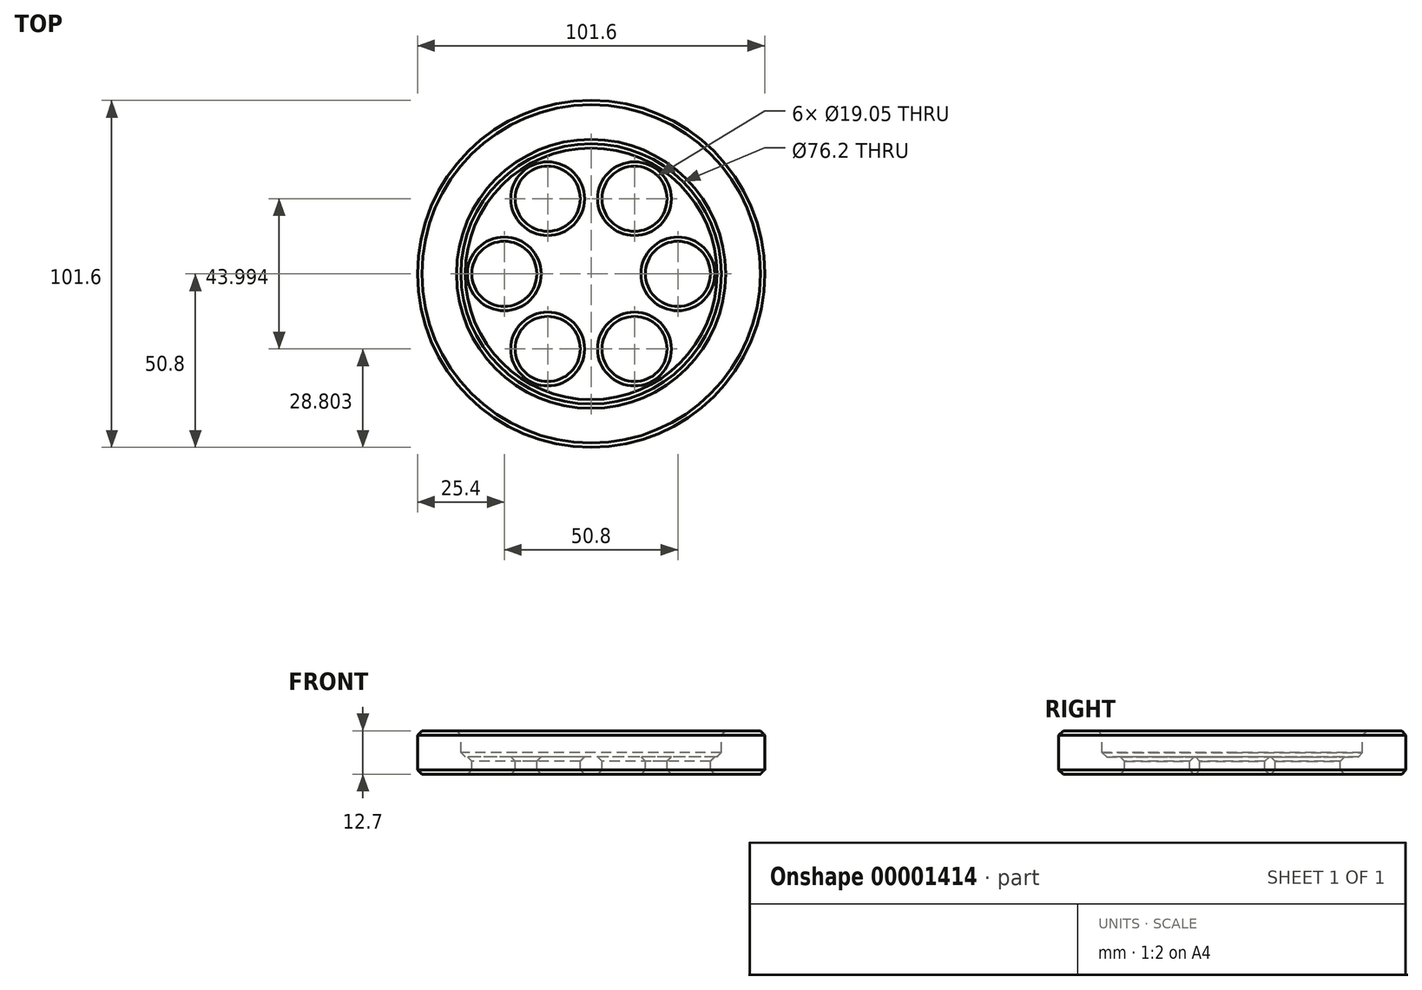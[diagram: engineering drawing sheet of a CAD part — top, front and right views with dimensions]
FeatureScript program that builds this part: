
annotation { "Feature Type Name" : "Feature", "Feature Type Description" : "" }
export const myFeature = defineFeature(function(context is Context, id is Id, definition is map)
    precondition{}
    {
        {
            var Q0;
            Q0=qCreatedBy(makeId("Top.planeOp"),FACE);
            var sketch = newSketch(context, id + "F0", { "sketchPlane" : qUnion([Q0])});
            skCircle(sketch, "E0", {"center": v(0, 0) * mm, "radius": 50.8 * mm});
            skSolve(sketch);
        }
        {
            var Q0;
            Q0 = qSketchRegion(id + "F0", true);
            extrude(context, id + "F1", {"entities" : qUnion([Q0]), "depth" : 12.7 * mm});
        }
        {
            var Q0;
            Q0=makeQuery(id+"F1.opExtrude","CAP_FACE",FACE,{"disambiguationData":[OSD([sQuery(id+"F0.wireOp",EDGE,"E0")])],"isStart":false});
            var sketch = newSketch(context, id + "F2", { "sketchPlane" : qUnion([Q0])});
            skCircle(sketch, "E1", {"center": v(0, 0) * mm, "radius": 38.1 * mm});
            skSolve(sketch);
        }
        {
            var Q0;
            Q0 = qSketchRegion(id + "F2", true);
            extrude(context, id + "F3", {"entities" : qUnion([Q0]), "operationType" : NewBodyOperationType.REMOVE, "oppositeDirection" : true, "depth" : 7.62 * mm});
        }
        {
            var Q0;
            Q0=makeQuery(id+"F3.boolean.opBoolean","COPY",FACE,{"derivedFrom":makeQuery(id+"F3.opExtrude","CAP_FACE",FACE,{"disambiguationData":[OSD([sQuery(id+"F2.wireOp",EDGE,"E1")])],"isStart":false})});
            var sketch = newSketch(context, id + "F4", { "sketchPlane" : qUnion([Q0])});
            skCircle(sketch, "E2.cCircle", {"center": v(0, 0) * mm, "radius": 22 * mm, "construction": true});
            skLineSegment(sketch, "E2.0", {"start": v(-12.7, 22) * mm, "end": v(12.7, 22) * mm, "construction": true});
            skLineSegment(sketch, "E2.1", {"start": v(12.7, 22) * mm, "end": v(25.4, 0) * mm, "construction": true});
            skLineSegment(sketch, "E2.2", {"start": v(25.4, 0) * mm, "end": v(12.7, -22) * mm, "construction": true});
            skLineSegment(sketch, "E2.3", {"start": v(12.7, -22) * mm, "end": v(-12.7, -22) * mm, "construction": true});
            skLineSegment(sketch, "E2.4", {"start": v(-12.7, -22) * mm, "end": v(-25.4, 0) * mm, "construction": true});
            skLineSegment(sketch, "E2.5", {"start": v(-25.4, 0) * mm, "end": v(-12.7, 22) * mm, "construction": true});
            skPoint(sketch, "E2.0.midPoint", {"position": v(0, 22) * mm});
            skCircle(sketch, "E3", {"center": v(-12.7, 22) * mm, "radius": 9.53 * mm});
            skCircle(sketch, "E4", {"center": v(12.7, 22) * mm, "radius": 9.53 * mm});
            skCircle(sketch, "E5", {"center": v(25.4, 0) * mm, "radius": 9.53 * mm});
            skCircle(sketch, "E6", {"center": v(12.7, -22) * mm, "radius": 9.53 * mm});
            skCircle(sketch, "E7", {"center": v(-12.7, -22) * mm, "radius": 9.53 * mm});
            skCircle(sketch, "E8", {"center": v(-25.4, 0) * mm, "radius": 9.53 * mm});
            skSolve(sketch);
        }
        {
            var Q0;
            Q0=makeQuery(id+"F4.imprint","IMPRINT",FACE,{"disambiguationData":[TD([[makeQuery(id+"F4.imprint","IMPRINT",EDGE,{"derivedFrom":sQuery(id+"F4.wireOp",EDGE,"E8")}),1.0]])]});
            var Q1;
            Q1=makeQuery(id+"F4.imprint","IMPRINT",FACE,{"disambiguationData":[TD([[makeQuery(id+"F4.imprint","IMPRINT",EDGE,{"derivedFrom":sQuery(id+"F4.wireOp",EDGE,"E3")}),1.0]])]});
            var Q2;
            Q2=makeQuery(id+"F4.imprint","IMPRINT",FACE,{"disambiguationData":[TD([[makeQuery(id+"F4.imprint","IMPRINT",EDGE,{"derivedFrom":sQuery(id+"F4.wireOp",EDGE,"E4")}),1.0]])]});
            var Q3;
            Q3=makeQuery(id+"F4.imprint","IMPRINT",FACE,{"disambiguationData":[TD([[makeQuery(id+"F4.imprint","IMPRINT",EDGE,{"derivedFrom":sQuery(id+"F4.wireOp",EDGE,"E5")}),1.0]])]});
            var Q4;
            Q4=makeQuery(id+"F4.imprint","IMPRINT",FACE,{"disambiguationData":[TD([[makeQuery(id+"F4.imprint","IMPRINT",EDGE,{"derivedFrom":sQuery(id+"F4.wireOp",EDGE,"E6")}),1.0]])]});
            var Q5;
            Q5=makeQuery(id+"F4.imprint","IMPRINT",FACE,{"disambiguationData":[TD([[makeQuery(id+"F4.imprint","IMPRINT",EDGE,{"derivedFrom":sQuery(id+"F4.wireOp",EDGE,"E7")}),1.0]])]});
            var Q6;
            Q6=sQuery(id+"F4.wireOp",EDGE,"E8");
            var Q7;
            Q7=sQuery(id+"F4.wireOp",EDGE,"E3");
            var Q8;
            Q8=sQuery(id+"F4.wireOp",EDGE,"E4");
            var Q9;
            Q9=sQuery(id+"F4.wireOp",EDGE,"E5");
            var Q10;
            Q10=sQuery(id+"F4.wireOp",EDGE,"E6");
            var Q11;
            Q11=sQuery(id+"F4.wireOp",EDGE,"E7");
            extrude(context, id + "F5", {"entities" : qUnion([Q0, Q1, Q2, Q3, Q4, Q5]), "operationType" : NewBodyOperationType.REMOVE, "surfaceEntities" : qUnion([Q6, Q7, Q8, Q9, Q10, Q11]), "oppositeDirection" : true, "depth" : 25.4 * mm});
        }
        {
            var Q0;
            Q0=makeQuery(id+"F1.opExtrude","CAP_FACE",FACE,{"disambiguationData":[OSD([sQuery(id+"F0.wireOp",EDGE,"E0")])],"isStart":false});
            var Q1;
            Q1=makeQuery(id+"F1.opExtrude","SWEPT_FACE",FACE,{"disambiguationData":[OSD([sQuery(id+"F0.wireOp",EDGE,"E0")])]});
            var Q2;
            Q2=makeQuery(id+"F3.boolean.opBoolean","COPY",FACE,{"derivedFrom":makeQuery(id+"F3.opExtrude","CAP_FACE",FACE,{"disambiguationData":[OSD([sQuery(id+"F2.wireOp",EDGE,"E1")])],"isStart":false})});
            var Q3;
            Q3=makeQuery(id+"F1.opExtrude","CAP_FACE",FACE,{"disambiguationData":[OSD([sQuery(id+"F0.wireOp",EDGE,"E0")])],"isStart":true});
            chamfer(context, id + "F6", {"entities" : qUnion([Q0, Q1, Q2, Q3]), "width" : 1.27 * mm, "tangentPropagation" : true});
        }
    });
